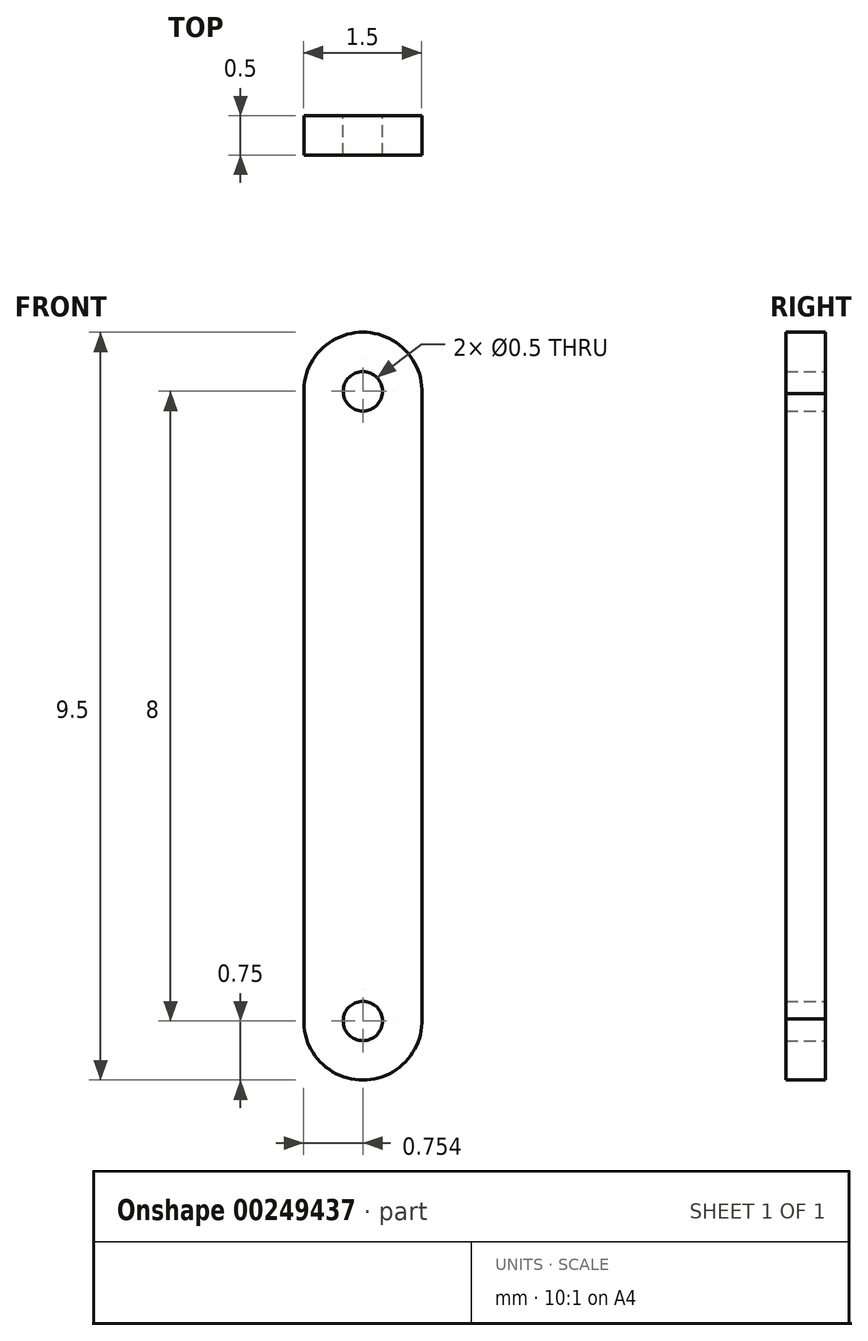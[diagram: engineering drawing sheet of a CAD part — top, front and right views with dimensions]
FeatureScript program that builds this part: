
annotation { "Feature Type Name" : "Feature", "Feature Type Description" : "" }
export const myFeature = defineFeature(function(context is Context, id is Id, definition is map)
    precondition{}
    {
        {
            var Q0;
            Q0=qCreatedBy(makeId("Front.planeOp"),FACE);
            var sketch = newSketch(context, id + "F0", { "sketchPlane" : qUnion([Q0])});
            skLineSegment(sketch, "E0.top", {"start": v(-25.18, 8.26) * mm, "end": v(-25.68, 8.26) * mm});
            skLineSegment(sketch, "E0.left", {"start": v(-25.18, 16.26) * mm, "end": v(-25.18, 8.26) * mm});
            skLineSegment(sketch, "E0.right", {"start": v(-26.68, 16.26) * mm, "end": v(-26.68, 8.26) * mm});
            skArc(sketch, "E1", {"start": v(-25.18, 16.2) * mm, "mid": v(-25.93, 16.98) * mm, "end": v(-26.68, 16.2) * mm});
            skPoint(sketch, "E1.third.point", {"position": v(-25.32, 15.78) * mm});
            skArc(sketch, "E2", {"start": v(-26.68, 8.26) * mm, "mid": v(-25.93, 7.48) * mm, "end": v(-25.18, 8.26) * mm});
            skPoint(sketch, "E2.third.point", {"position": v(-25.42, 7.68) * mm});
            skCircle(sketch, "E3", {"center": v(-25.93, 16.23) * mm, "radius": 0.25 * mm});
            skCircle(sketch, "E4", {"center": v(-25.93, 8.23) * mm, "radius": 0.25 * mm});
            skLineSegment(sketch, "E5.trimOffspring", {"start": v(-26.17, 8.26) * mm, "end": v(-26.68, 8.26) * mm});
            skSolve(sketch);
        }
        {
            var Q0;
            {var subQ1=sQuery(id+"F0.wireOp",EDGE,"E0.left");var subQ4=sQuery(id+"F0.wireOp",EDGE,"E1");var subQ5=makeQuery(id+"F0.imprint","INTERSECT",VERTEX,{"derivedFrom":[subQ1,subQ4]});Q0=makeQuery(id+"F0.imprint","IMPRINT",FACE,{"disambiguationData":[TD([[makeQuery(id+"F0.imprint","IMPRINT",EDGE,{"disambiguationData":[TD([[subQ5,1.0]])],"derivedFrom":subQ4}),-1.0]])]});}
            var Q1;
            {var subQ0=sQuery(id+"F0.wireOp",EDGE,"E0.top");Q1=makeQuery(id+"F0.imprint","IMPRINT",FACE,{"disambiguationData":[TD([[makeQuery(id+"F0.imprint","IMPRINT",EDGE,{"derivedFrom":subQ0}),1.0]])]});}
            var Q2;
            {var subQ0=sQuery(id+"F0.wireOp",EDGE,"E0.top");Q2=makeQuery(id+"F0.imprint","IMPRINT",FACE,{"disambiguationData":[TD([[makeQuery(id+"F0.imprint","IMPRINT",EDGE,{"derivedFrom":subQ0}),-1.0]])]});}
            var Q3;
            {var subQ0=sQuery(id+"F0.wireOp",EDGE,"E0.bottom");Q3=makeQuery(id+"F0.imprint","IMPRINT",FACE,{"disambiguationData":[TD([[makeQuery(id+"F0.imprint","IMPRINT",EDGE,{"derivedFrom":subQ0}),1.0]])]});}
            var Q4;
            {var subQ0=sQuery(id+"F0.wireOp",EDGE,"E0.bottom");Q4=makeQuery(id+"F0.imprint","IMPRINT",FACE,{"disambiguationData":[TD([[makeQuery(id+"F0.imprint","IMPRINT",EDGE,{"derivedFrom":subQ0}),-1.0]])]});}
            var Q5;
            {var subQ0=sQuery(id+"F0.wireOp",EDGE,"E1");var subQ1=sQuery(id+"F0.wireOp",EDGE,"E0.left");var subQ3=makeQuery(id+"F0.imprint","INTERSECT",VERTEX,{"derivedFrom":[subQ1,subQ0]});Q5=makeQuery(id+"F0.imprint","IMPRINT",FACE,{"disambiguationData":[TD([[makeQuery(id+"F0.imprint","IMPRINT",EDGE,{"disambiguationData":[TD([[subQ3,1.0]])],"derivedFrom":subQ1}),1.0]])]});}
            var Q6;
            {var subQ0=sQuery(id+"F0.wireOp",EDGE,"E1");var subQ1=sQuery(id+"F0.wireOp",EDGE,"E0.right");var subQ3=makeQuery(id+"F0.imprint","INTERSECT",VERTEX,{"derivedFrom":[subQ1,subQ0]});Q6=makeQuery(id+"F0.imprint","IMPRINT",FACE,{"disambiguationData":[TD([[makeQuery(id+"F0.imprint","IMPRINT",EDGE,{"disambiguationData":[TD([[subQ3,1.0]])],"derivedFrom":subQ1}),-1.0]])]});}
            extrude(context, id + "F1", {"entities" : qUnion([Q0, Q1, Q2, Q3, Q4, Q5, Q6]), "depth" : .5 * mm});
        }
    });
